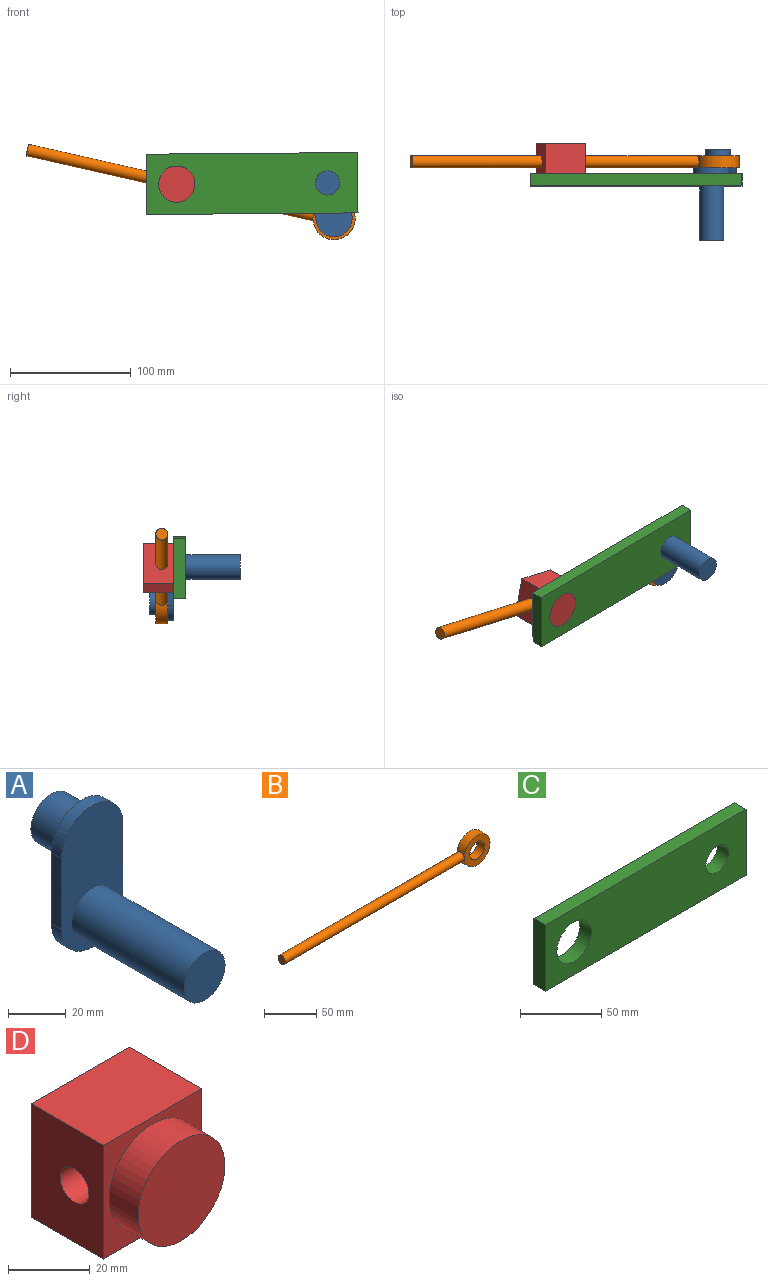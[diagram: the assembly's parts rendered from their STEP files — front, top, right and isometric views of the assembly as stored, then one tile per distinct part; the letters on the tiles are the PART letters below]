
ASSEMBLY  parts=4 mates=4
PART A: 10 faces, bbox 30x75x60 mm
  f0: cylinder r=15mm len=30mm, axis (0,1,0), area 235.6mm2, adj f1,f3,f4,f5
  f1: plane 30x5mm, normal (-1,0,0), area 150mm2, adj f0,f2,f4,f5
  f2: cylinder r=15mm len=30mm, axis (0,1,0), area 235.6mm2, adj f1,f3,f4,f5
  f3: plane 30x5mm, normal (1,0,0), area 150mm2, adj f0,f2,f4,f5
  f4: plane 60x30mm, normal (0,-1,0), area 1292.7mm2, adj f0,f1,f2,f3,f8
  f5: plane 60x30mm, normal (0,1,0), area 1292.7mm2, adj f0,f1,f2,f3,f6
  f6: cylinder r=10mm len=20mm, axis (0,-1,0), area 942.5mm2, adj f5,f7
  f7: plane 20x20mm, normal (0,1,0), area 314.2mm2, adj f6
  f8: cylinder r=10mm len=55mm, axis (0,1,0), area 3455.8mm2, adj f4,f9
  f9: plane 20x20mm, normal (0,-1,0), area 314.2mm2, adj f8
PART B: 6 faces, bbox 277.9x10x35 mm
  f0: cylinder r=10mm len=20mm, axis (0,-1,0), area 628.3mm2, adj f2,f3
  f1: cylinder r=17.5mm len=35mm, axis (0,-1,0), area 1020mm2, adj f2,f3,f4
  f2: plane 35x35mm, normal (0,1,0), area 648mm2, adj f0,f1
  f3: plane 35x35mm, normal (0,-1,0), area 648mm2, adj f0,f1
  f4: cylinder r=5mm len=243.95mm, axis (-1,0,0), area 7642.9mm2, adj f1,f5
  f5: plane 10x10mm, normal (-1,0,0), area 78.5mm2, adj f4
PART C: 8 faces, bbox 175x10x50 mm
  f0: plane 50x10mm, normal (-1,0,0), area 500mm2, adj f1,f4,f6,f7
  f1: plane 175x10mm, normal (0,0,-1), area 1750mm2, adj f0,f2,f6,f7
  f2: plane 50x10mm, normal (1,0,0), area 500mm2, adj f1,f4,f6,f7
  f3: cylinder r=10mm len=20mm, axis (0,1,0), area 628.3mm2, adj f6,f7
  f4: plane 175x10mm, normal (0,0,1), area 1750mm2, adj f0,f2,f6,f7
  f5: cylinder r=15mm len=30mm, axis (0,1,0), area 942.5mm2, adj f6,f7
  f6: plane 175x50mm, normal (0,-1,0), area 7729mm2, adj f0,f1,f2,f3,f4,f5
  f7: plane 175x50mm, normal (0,1,0), area 7729mm2, adj f0,f1,f2,f3,f4,f5
PART D: 9 faces, bbox 34x35x34 mm
  f0: cylinder r=15mm len=30mm, axis (0,1,0), area 942.5mm2, adj f1,f7
  f1: plane 30x30mm, normal (0,-1,0), area 706.9mm2, adj f0
  f2: plane 34x25mm, normal (0,0,1), area 850mm2, adj f3,f5,f6,f7
  f3: plane 34x25mm, normal (-1,0,0), area 771.5mm2, adj f2,f4,f6,f7,f8
  f4: plane 34x25mm, normal (0,0,-1), area 850mm2, adj f3,f5,f6,f7
  f5: plane 34x25mm, normal (1,0,0), area 771.5mm2, adj f2,f4,f6,f7,f8
  f6: plane 34x34mm, normal (0,1,0), area 1156mm2, adj f2,f3,f4,f5
  f7: plane 34x34mm, normal (0,-1,0), area 449.1mm2, adj f0,f2,f3,f4,f5
  f8: cylinder r=5mm len=34mm, axis (-1,0,0), area 1068.1mm2, adj f3,f5
PLACE A rot(axis=(0,1,0),169.7deg) t=(-195.12,5,-112.32)mm
PLACE B rot(axis=(0,1,0),12.8deg) t=(-129.87,5,-124.73)mm
PLACE C rot(axis=(0,-1,0),0.4deg) t=(-3.83,0,-23.69)mm fixed
PLACE D rot(axis=(0,1,0),12.8deg) t=(-170.4,0,-185.34)mm
MATE revolute B.f0 <-> A.f0  axis (0,-1,0) through (-189.76,5,-141.84)mm
MATE revolute D.f0 <-> C.f5  axis (0,1,0) through (-320.12,0,-113.28)mm
MATE slider D.f8 <-> B.f4  axis (-0.98,0,0.22) through (-303.54,10,-117.05)mm
MATE revolute A.f8 <-> C.f3  axis (0,1,0) through (-195.12,0,-112.32)mm
